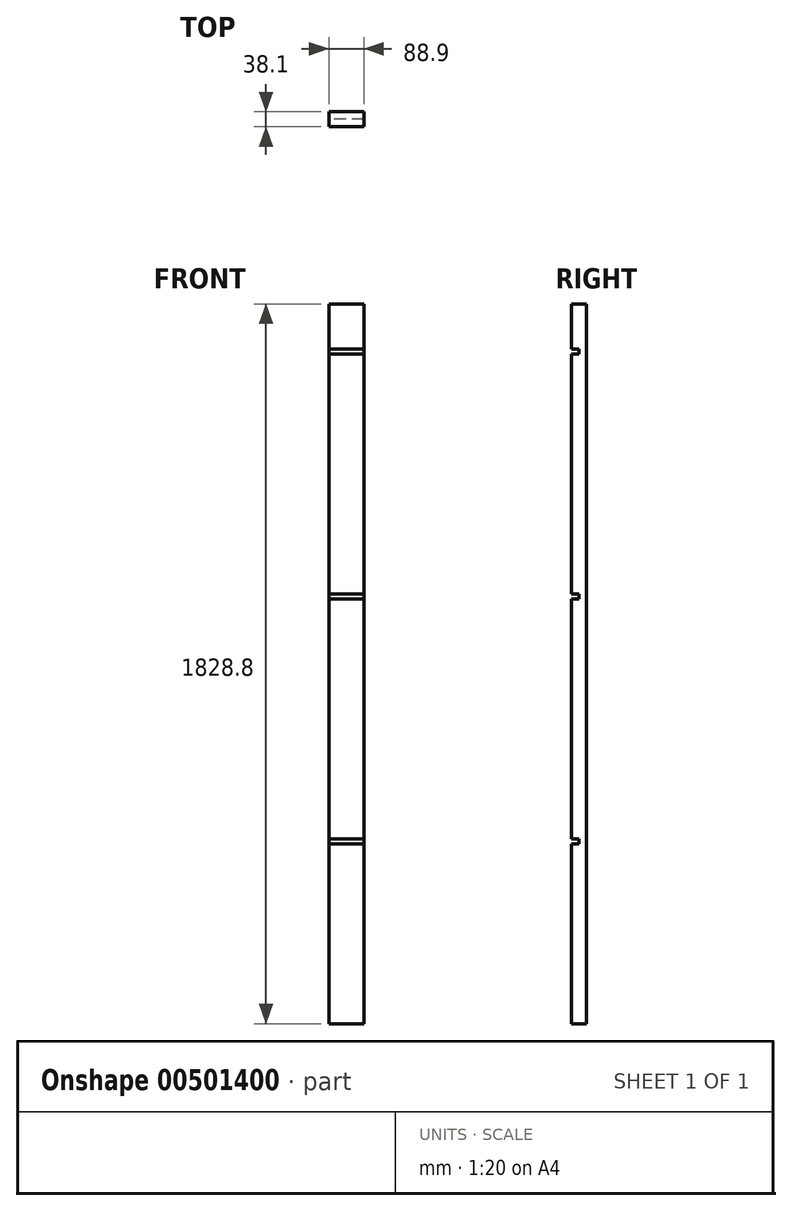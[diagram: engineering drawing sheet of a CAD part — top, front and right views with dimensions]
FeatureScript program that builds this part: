
annotation { "Feature Type Name" : "Feature", "Feature Type Description" : "" }
export const myFeature = defineFeature(function(context is Context, id is Id, definition is map)
    precondition{}
    {
        {
            var Q0;
            Q0=qCreatedBy(makeId("Front.planeOp"),FACE);
            var sketch = newSketch(context, id + "F0", { "sketchPlane" : qUnion([Q0])});
            skLineSegment(sketch, "E0.bottom", {"start": v(0, 0) * mm, "end": v(88.9, 0) * mm});
            skLineSegment(sketch, "E0.top", {"start": v(0, 1828.8) * mm, "end": v(88.9, 1828.8) * mm});
            skLineSegment(sketch, "E0.left", {"start": v(0, 0) * mm, "end": v(0, 1828.8) * mm});
            skLineSegment(sketch, "E0.right", {"start": v(88.9, 0) * mm, "end": v(88.9, 1828.8) * mm});
            skSolve(sketch);
        }
        {
            var Q0;
            Q0=makeQuery(id+"F0.imprint","IMPRINT",FACE,{"disambiguationData":[TD([[makeQuery(id+"F0.imprint","IMPRINT",EDGE,{"derivedFrom":sQuery(id+"F0.wireOp",EDGE,"E0.bottom")}),1.0]])]});
            extrude(context, id + "F1", {"entities" : qUnion([Q0]), "depth" : 38.1 * mm});
        }
        {
            var Q0;
            Q0=makeQuery(id+"F1.opExtrude","SWEPT_FACE",FACE,{"disambiguationData":[OSD([sQuery(id+"F0.wireOp",EDGE,"E0.left")])]});
            var sketch = newSketch(context, id + "F2", { "sketchPlane" : qUnion([Q0])});
            skLineSegment(sketch, "E1.bottom", {"start": v(38.1, 1714.5) * mm, "end": v(19.05, 1714.5) * mm});
            skLineSegment(sketch, "E1.top", {"start": v(38.1, 1701.8) * mm, "end": v(19.05, 1701.8) * mm});
            skLineSegment(sketch, "E1.left", {"start": v(38.1, 1714.5) * mm, "end": v(38.1, 1701.8) * mm});
            skLineSegment(sketch, "E1.right", {"start": v(19.05, 1714.5) * mm, "end": v(19.05, 1701.8) * mm});
            skLineSegment(sketch, "E2.bottom", {"start": v(38.1, 1092.2) * mm, "end": v(19.05, 1092.2) * mm});
            skLineSegment(sketch, "E2.top", {"start": v(38.1, 1079.5) * mm, "end": v(19.05, 1079.5) * mm});
            skLineSegment(sketch, "E2.left", {"start": v(38.1, 1092.2) * mm, "end": v(38.1, 1079.5) * mm});
            skLineSegment(sketch, "E2.right", {"start": v(19.05, 1092.2) * mm, "end": v(19.05, 1079.5) * mm});
            skLineSegment(sketch, "E3.bottom", {"start": v(38.1, 469.9) * mm, "end": v(19.05, 469.9) * mm});
            skLineSegment(sketch, "E3.top", {"start": v(38.1, 457.2) * mm, "end": v(19.05, 457.2) * mm});
            skLineSegment(sketch, "E3.left", {"start": v(38.1, 469.9) * mm, "end": v(38.1, 457.2) * mm});
            skLineSegment(sketch, "E3.right", {"start": v(19.05, 469.9) * mm, "end": v(19.05, 457.2) * mm});
            skSolve(sketch);
        }
        {
            var Q0;
            Q0 = qSketchRegion(id + "F2", true);
            extrude(context, id + "F3", {"entities" : qUnion([Q0]), "operationType" : NewBodyOperationType.REMOVE, "endBound" : BoundingType.UP_TO_NEXT, "oppositeDirection" : true, "depth" : 25.4 * mm});
        }
    });
